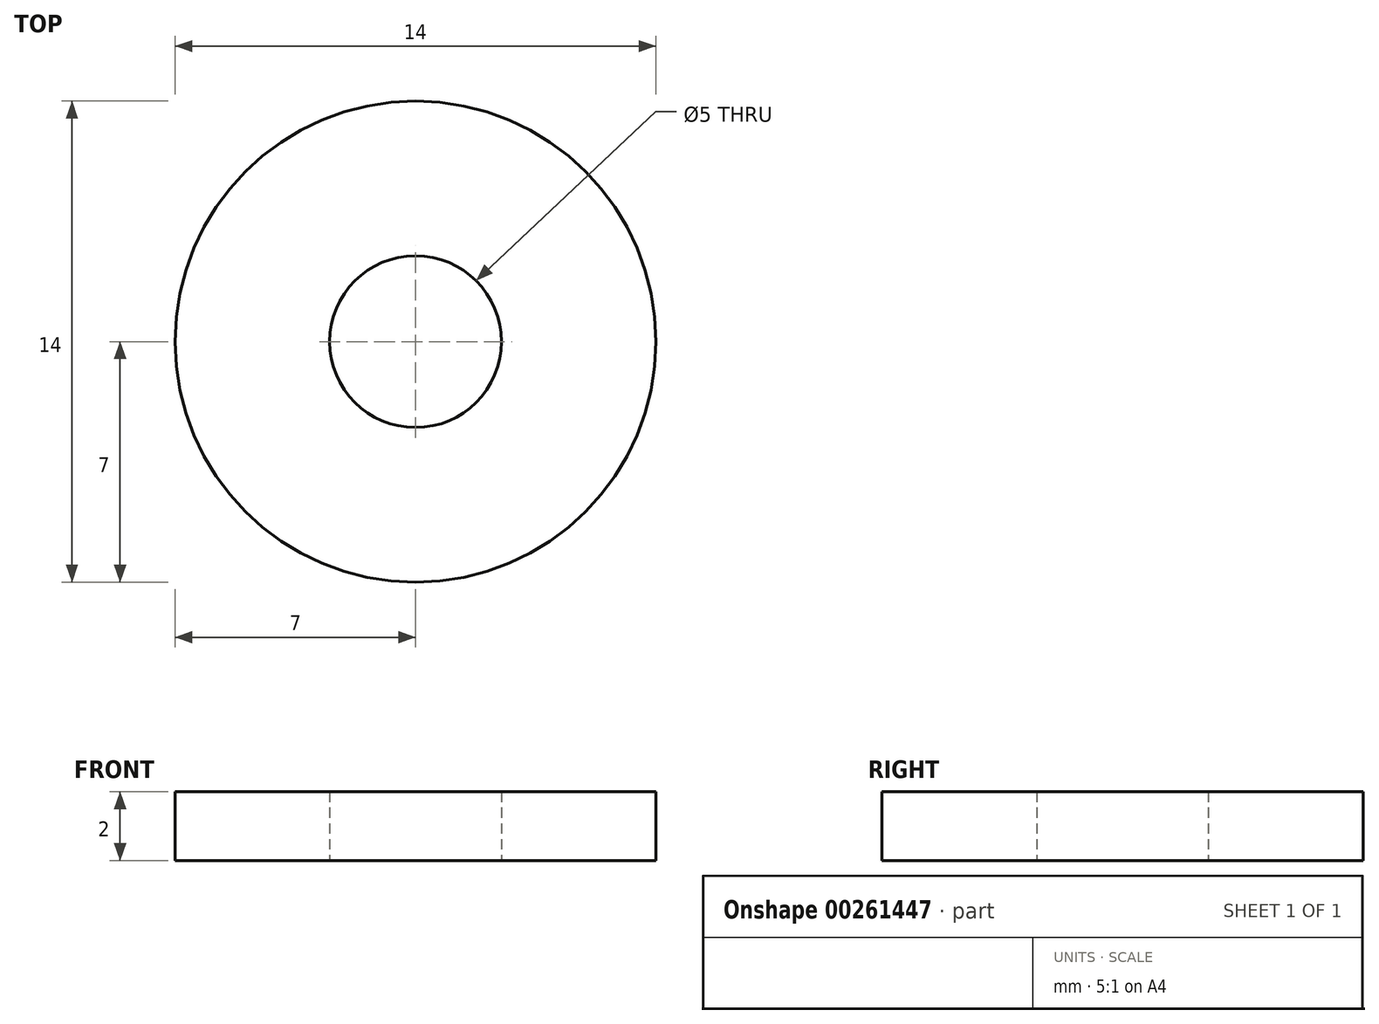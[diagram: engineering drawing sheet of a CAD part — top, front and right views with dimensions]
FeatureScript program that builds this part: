
annotation { "Feature Type Name" : "Feature", "Feature Type Description" : "" }
export const myFeature = defineFeature(function(context is Context, id is Id, definition is map)
    precondition{}
    {
        {
            var Q0;
            Q0=qCreatedBy(makeId("Top.planeOp"),FACE);
            var sketch = newSketch(context, id + "F0", { "sketchPlane" : qUnion([Q0])});
            skCircle(sketch, "E0", {"center": v(0, 0) * mm, "radius": 2.5 * mm});
            skCircle(sketch, "E1", {"center": v(0, 0) * mm, "radius": 7 * mm});
            skSolve(sketch);
        }
        {
            var Q0;
            Q0 = qSketchRegion(id + "F0", true);
            extrude(context, id + "F1", {"entities" : qUnion([Q0]), "depth" : 2 * mm});
        }
    });
